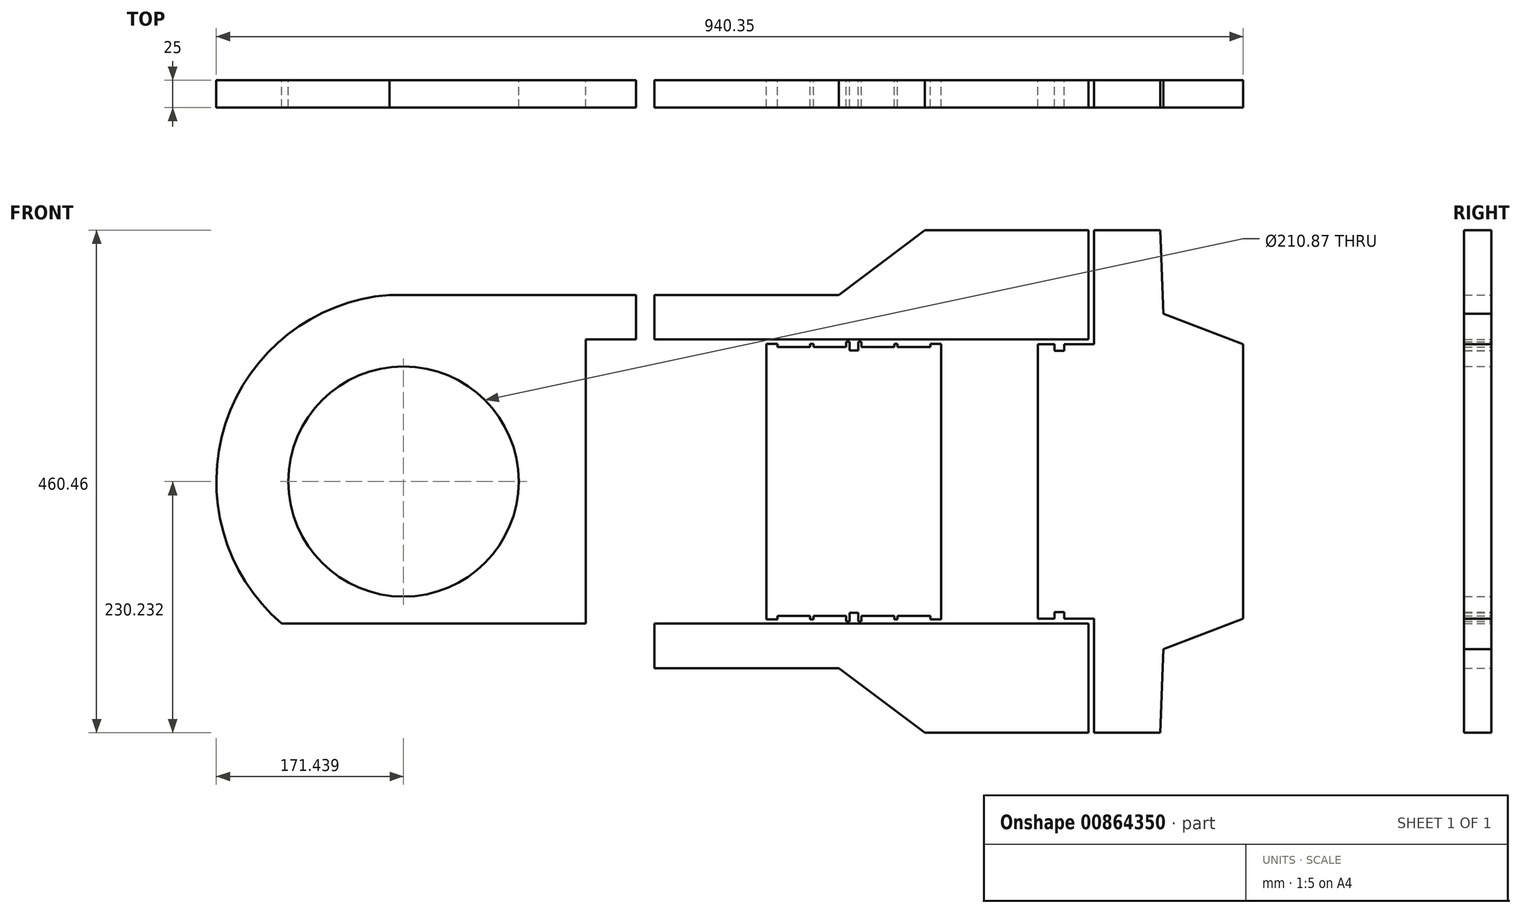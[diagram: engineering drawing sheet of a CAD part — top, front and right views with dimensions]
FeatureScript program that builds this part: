
annotation { "Feature Type Name" : "Feature", "Feature Type Description" : "" }
export const myFeature = defineFeature(function(context is Context, id is Id, definition is map)
    precondition{}
    {
        {
            var Q0;
            Q0=qCreatedBy(makeId("Front.planeOp"),FACE);
            var sketch = newSketch(context, id + "F0", { "sketchPlane" : qUnion([Q0])});
            skLineSegment(sketch, "E0", {"start": v(0, 0) * mm, "end": v(1000, 0) * mm});
            skLineSegment(sketch, "E1", {"start": v(1000, 0) * mm, "end": v(1000, 100) * mm});
            skLineSegment(sketch, "E2", {"start": v(1000, 100) * mm, "end": v(850, 100) * mm});
            skLineSegment(sketch, "E3", {"start": v(850, 100) * mm, "end": v(771.4, 40.72) * mm});
            skLineSegment(sketch, "E4", {"start": v(771.4, 40.72) * mm, "end": v(0, 40.72) * mm});
            skLineSegment(sketch, "E5", {"start": v(0, 40.72) * mm, "end": v(0, 0) * mm});
            skLineSegment(sketch, "E6", {"start": v(0, -130.23) * mm, "end": v(1152.59, -130.23) * mm, "construction": true});
            skLineSegment(sketch, "E7.MirrorCS", {"start": v(771.4, -301.17) * mm, "end": v(0, -301.17) * mm});
            skLineSegment(sketch, "E8.MirrorCS", {"start": v(0, -260.46) * mm, "end": v(1000, -260.46) * mm});
            skLineSegment(sketch, "E9.MirrorCS", {"start": v(0, -301.17) * mm, "end": v(0, -260.46) * mm});
            skLineSegment(sketch, "E10.MirrorCS", {"start": v(850, -360.46) * mm, "end": v(771.4, -301.17) * mm});
            skLineSegment(sketch, "E11.MirrorCS", {"start": v(1000, -360.46) * mm, "end": v(850, -360.46) * mm});
            skLineSegment(sketch, "E12.MirrorCS", {"start": v(1000, -260.46) * mm, "end": v(1000, -360.46) * mm});
            skLineSegment(sketch, "E13", {"start": v(953.7, -130.23) * mm, "end": v(953.7, -4.47) * mm});
            skLineSegment(sketch, "E14", {"start": v(953.7, -4.47) * mm, "end": v(968.7, -4.47) * mm});
            skLineSegment(sketch, "E15", {"start": v(968.7, -4.47) * mm, "end": v(968.7, -10.47) * mm});
            skLineSegment(sketch, "E16", {"start": v(968.7, -10.47) * mm, "end": v(977.7, -10.47) * mm});
            skLineSegment(sketch, "E17", {"start": v(977.7, -10.47) * mm, "end": v(977.7, -4.47) * mm});
            skLineSegment(sketch, "E18", {"start": v(977.7, -4.47) * mm, "end": v(1005, -4.47) * mm});
            skLineSegment(sketch, "E19", {"start": v(1005, -4.47) * mm, "end": v(1005, 100) * mm});
            skLineSegment(sketch, "E20", {"start": v(1005, 100) * mm, "end": v(1065.83, 100) * mm});
            skLineSegment(sketch, "E21", {"start": v(1065.83, 100) * mm, "end": v(1068.65, 23.42) * mm});
            skLineSegment(sketch, "E22", {"start": v(1068.65, 23.42) * mm, "end": v(1141.62, -4.47) * mm});
            skLineSegment(sketch, "E23", {"start": v(1141.62, -4.47) * mm, "end": v(1141.62, -130.23) * mm});
            skLineSegment(sketch, "E24.MirrorCS", {"start": v(968.7, -255.99) * mm, "end": v(968.7, -249.99) * mm});
            skLineSegment(sketch, "E25.MirrorCS", {"start": v(968.7, -249.99) * mm, "end": v(977.7, -249.99) * mm});
            skLineSegment(sketch, "E26.MirrorCS", {"start": v(977.7, -249.99) * mm, "end": v(977.7, -255.99) * mm});
            skLineSegment(sketch, "E27.MirrorCS", {"start": v(953.7, -255.99) * mm, "end": v(968.7, -255.99) * mm});
            skLineSegment(sketch, "E28.MirrorCS", {"start": v(977.7, -255.99) * mm, "end": v(1005, -255.99) * mm});
            skLineSegment(sketch, "E29.MirrorCS", {"start": v(1141.62, -255.99) * mm, "end": v(1141.62, -130.23) * mm});
            skLineSegment(sketch, "E30.MirrorCS", {"start": v(953.7, -130.23) * mm, "end": v(953.7, -255.99) * mm});
            skLineSegment(sketch, "E31.MirrorCS", {"start": v(1005, -360.46) * mm, "end": v(1065.83, -360.46) * mm});
            skLineSegment(sketch, "E32.MirrorCS", {"start": v(1065.83, -360.46) * mm, "end": v(1068.65, -283.87) * mm});
            skLineSegment(sketch, "E33.MirrorCS", {"start": v(1068.65, -283.87) * mm, "end": v(1141.62, -255.99) * mm});
            skLineSegment(sketch, "E34.MirrorCS", {"start": v(1005, -255.99) * mm, "end": v(1005, -360.46) * mm});
            skLineSegment(sketch, "E35", {"start": v(705.08, -130.23) * mm, "end": v(705.08, -4.06) * mm});
            skLineSegment(sketch, "E36", {"start": v(705.08, -4.06) * mm, "end": v(715.08, -4.06) * mm});
            skLineSegment(sketch, "E37", {"start": v(715.08, -4.06) * mm, "end": v(715.08, -7.06) * mm});
            skLineSegment(sketch, "E38", {"start": v(715.08, -7.06) * mm, "end": v(745.08, -7.06) * mm});
            skLineSegment(sketch, "E39", {"start": v(745.08, -7.06) * mm, "end": v(745.08, -4.06) * mm});
            skLineSegment(sketch, "E40", {"start": v(745.08, -4.06) * mm, "end": v(748.08, -4.06) * mm});
            skLineSegment(sketch, "E41", {"start": v(748.08, -4.06) * mm, "end": v(748.08, -7.06) * mm});
            skLineSegment(sketch, "E42", {"start": v(748.08, -7.06) * mm, "end": v(778.08, -7.06) * mm});
            skLineSegment(sketch, "E43", {"start": v(778.08, -7.06) * mm, "end": v(778.08, -2.06) * mm});
            skLineSegment(sketch, "E44", {"start": v(778.08, -2.06) * mm, "end": v(781.08, -2.06) * mm});
            skLineSegment(sketch, "E45", {"start": v(781.08, -2.06) * mm, "end": v(781.08, -10.06) * mm});
            skLineSegment(sketch, "E46", {"start": v(781.08, -10.06) * mm, "end": v(789.08, -10.06) * mm});
            skLineSegment(sketch, "E47", {"start": v(789.08, -10.06) * mm, "end": v(789.08, -2.06) * mm});
            skLineSegment(sketch, "E48", {"start": v(789.08, -2.06) * mm, "end": v(792.08, -2.06) * mm});
            skLineSegment(sketch, "E49", {"start": v(792.08, -2.06) * mm, "end": v(792.08, -7.06) * mm});
            skLineSegment(sketch, "E50", {"start": v(792.08, -7.06) * mm, "end": v(822.08, -7.06) * mm});
            skLineSegment(sketch, "E51", {"start": v(822.08, -7.06) * mm, "end": v(822.08, -4.06) * mm});
            skLineSegment(sketch, "E52", {"start": v(822.08, -4.06) * mm, "end": v(825.08, -4.06) * mm});
            skLineSegment(sketch, "E53", {"start": v(825.08, -4.06) * mm, "end": v(825.08, -7.06) * mm});
            skLineSegment(sketch, "E54", {"start": v(825.08, -7.06) * mm, "end": v(855.08, -7.06) * mm});
            skLineSegment(sketch, "E55", {"start": v(855.08, -7.06) * mm, "end": v(855.08, -4.06) * mm});
            skLineSegment(sketch, "E56", {"start": v(855.08, -4.06) * mm, "end": v(865.08, -4.06) * mm});
            skLineSegment(sketch, "E57", {"start": v(865.08, -4.06) * mm, "end": v(865.08, -130.23) * mm});
            skLineSegment(sketch, "E58.MirrorCS", {"start": v(855.08, -253.4) * mm, "end": v(855.08, -256.4) * mm});
            skLineSegment(sketch, "E59.MirrorCS", {"start": v(715.08, -256.4) * mm, "end": v(715.08, -253.4) * mm});
            skLineSegment(sketch, "E60.MirrorCS", {"start": v(789.08, -258.4) * mm, "end": v(792.08, -258.4) * mm});
            skLineSegment(sketch, "E61.MirrorCS", {"start": v(748.08, -256.4) * mm, "end": v(748.08, -253.4) * mm});
            skLineSegment(sketch, "E62.MirrorCS", {"start": v(822.08, -256.4) * mm, "end": v(825.08, -256.4) * mm});
            skLineSegment(sketch, "E63.MirrorCS", {"start": v(825.08, -256.4) * mm, "end": v(825.08, -253.4) * mm});
            skLineSegment(sketch, "E64.MirrorCS", {"start": v(822.08, -253.4) * mm, "end": v(822.08, -256.4) * mm});
            skLineSegment(sketch, "E65.MirrorCS", {"start": v(778.08, -258.4) * mm, "end": v(781.08, -258.4) * mm});
            skLineSegment(sketch, "E66.MirrorCS", {"start": v(745.08, -256.4) * mm, "end": v(748.08, -256.4) * mm});
            skLineSegment(sketch, "E67.MirrorCS", {"start": v(745.08, -253.4) * mm, "end": v(745.08, -256.4) * mm});
            skLineSegment(sketch, "E68.MirrorCS", {"start": v(789.08, -250.4) * mm, "end": v(789.08, -258.4) * mm});
            skLineSegment(sketch, "E69.MirrorCS", {"start": v(748.08, -253.4) * mm, "end": v(778.08, -253.4) * mm});
            skLineSegment(sketch, "E70.MirrorCS", {"start": v(705.08, -256.4) * mm, "end": v(715.08, -256.4) * mm});
            skLineSegment(sketch, "E71.MirrorCS", {"start": v(781.08, -250.4) * mm, "end": v(789.08, -250.4) * mm});
            skLineSegment(sketch, "E72.MirrorCS", {"start": v(825.08, -253.4) * mm, "end": v(855.08, -253.4) * mm});
            skLineSegment(sketch, "E73.MirrorCS", {"start": v(865.08, -256.4) * mm, "end": v(865.08, -130.23) * mm});
            skLineSegment(sketch, "E74.MirrorCS", {"start": v(792.08, -253.4) * mm, "end": v(822.08, -253.4) * mm});
            skLineSegment(sketch, "E75.MirrorCS", {"start": v(705.08, -130.23) * mm, "end": v(705.08, -256.4) * mm});
            skLineSegment(sketch, "E76.MirrorCS", {"start": v(781.08, -258.4) * mm, "end": v(781.08, -250.4) * mm});
            skLineSegment(sketch, "E77.MirrorCS", {"start": v(792.08, -258.4) * mm, "end": v(792.08, -253.4) * mm});
            skLineSegment(sketch, "E78.MirrorCS", {"start": v(855.08, -256.4) * mm, "end": v(865.08, -256.4) * mm});
            skLineSegment(sketch, "E79.MirrorCS", {"start": v(778.08, -253.4) * mm, "end": v(778.08, -258.4) * mm});
            skLineSegment(sketch, "E80.MirrorCS", {"start": v(715.08, -253.4) * mm, "end": v(745.08, -253.4) * mm});
            skLineSegment(sketch, "E81.bottom", {"start": v(-11.91, 107.98) * mm, "end": v(602.46, 107.98) * mm});
            skLineSegment(sketch, "E81.top", {"start": v(-11.91, -371.28) * mm, "end": v(602.46, -371.28) * mm});
            skLineSegment(sketch, "E81.left", {"start": v(-11.91, 107.98) * mm, "end": v(-11.91, -371.28) * mm});
            skLineSegment(sketch, "E81.right", {"start": v(602.46, 107.98) * mm, "end": v(602.46, -371.28) * mm});
            skLineSegment(sketch, "E82", {"start": v(585.7, 40.72) * mm, "end": v(585.7, 0) * mm});
            skLineSegment(sketch, "E83", {"start": v(585.7, 0) * mm, "end": v(539.53, 0) * mm});
            skLineSegment(sketch, "E84", {"start": v(539.53, 0) * mm, "end": v(539.53, -260.46) * mm});
            skLineSegment(sketch, "E85", {"start": v(539.53, -260.46) * mm, "end": v(585.7, -260.46) * mm});
            skLineSegment(sketch, "E86", {"start": v(585.7, -260.46) * mm, "end": v(585.7, -301.17) * mm});
            skLineSegment(sketch, "E87", {"start": v(585.7, -301.17) * mm, "end": v(385.7, -301.17) * mm});
            skLineSegment(sketch, "E88", {"start": v(585.7, 40.72) * mm, "end": v(385.7, 40.72) * mm});
            skArc(sketch, "E89", {"start": v(385.7, 40.72) * mm, "mid": v(201.27, -130.23) * mm, "end": v(385.7, -301.17) * mm});
            skCircle(sketch, "E90", {"center": v(372.7, -130.23) * mm, "radius": 105.44 * mm});
            skSolve(sketch);
        }
        {
            var Q0;
            Q0=makeQuery(id+"F0.imprint","IMPRINT",FACE,{"disambiguationData":[TD([[makeQuery(id+"F0.imprint","IMPRINT",EDGE,{"derivedFrom":sQuery(id+"F0.wireOp",EDGE,"E35")}),-1.0]])]});
            var Q1;
            Q1=makeQuery(id+"F0.imprint","IMPRINT",FACE,{"disambiguationData":[TD([[makeQuery(id+"F0.imprint","IMPRINT",EDGE,{"derivedFrom":sQuery(id+"F0.wireOp",EDGE,"E11.MirrorCS")}),-1.0]])]});
            var Q2;
            Q2=makeQuery(id+"F0.imprint","IMPRINT",FACE,{"disambiguationData":[TD([[makeQuery(id+"F0.imprint","IMPRINT",EDGE,{"derivedFrom":sQuery(id+"F0.wireOp",EDGE,"E13")}),-1.0]])]});
            var Q3;
            {var subQ1=sQuery(id+"F0.wireOp",EDGE,"E1");Q3=makeQuery(id+"F0.imprint","IMPRINT",FACE,{"disambiguationData":[TD([[makeQuery(id+"F0.imprint","IMPRINT",EDGE,{"derivedFrom":subQ1}),1.0]])]});}
            extrude(context, id + "F1", {"entities" : qUnion([Q0, Q1, Q2, Q3]), "depth" : 25 * mm, "offsetDistance" : 25 * mm});
        }
        {
            var Q0;
            {var subQ5=sQuery(id+"F0.wireOp",EDGE,"E84");Q0=makeQuery(id+"F0.imprint","IMPRINT",FACE,{"disambiguationData":[TD([[makeQuery(id+"F0.imprint","IMPRINT",EDGE,{"derivedFrom":subQ5}),-1.0]])]});}
            var Q1;
            Q1=makeQuery(id+"F0.imprint","IMPRINT",FACE,{"disambiguationData":[TD([[makeQuery(id+"F0.imprint","IMPRINT",EDGE,{"derivedFrom":sQuery(id+"F0.wireOp",EDGE,"E82")}),-1.0]])]});
            var Q2;
            {var subQ0=sQuery(id+"F0.wireOp",EDGE,"E85");Q2=makeQuery(id+"F0.imprint","IMPRINT",FACE,{"disambiguationData":[TD([[makeQuery(id+"F0.imprint","IMPRINT",EDGE,{"derivedFrom":subQ0}),-1.0]])]});}
            extrude(context, id + "F2", {"entities" : qUnion([Q0, Q1, Q2]), "depth" : 25 * mm, "offsetDistance" : 25 * mm});
        }
    });
